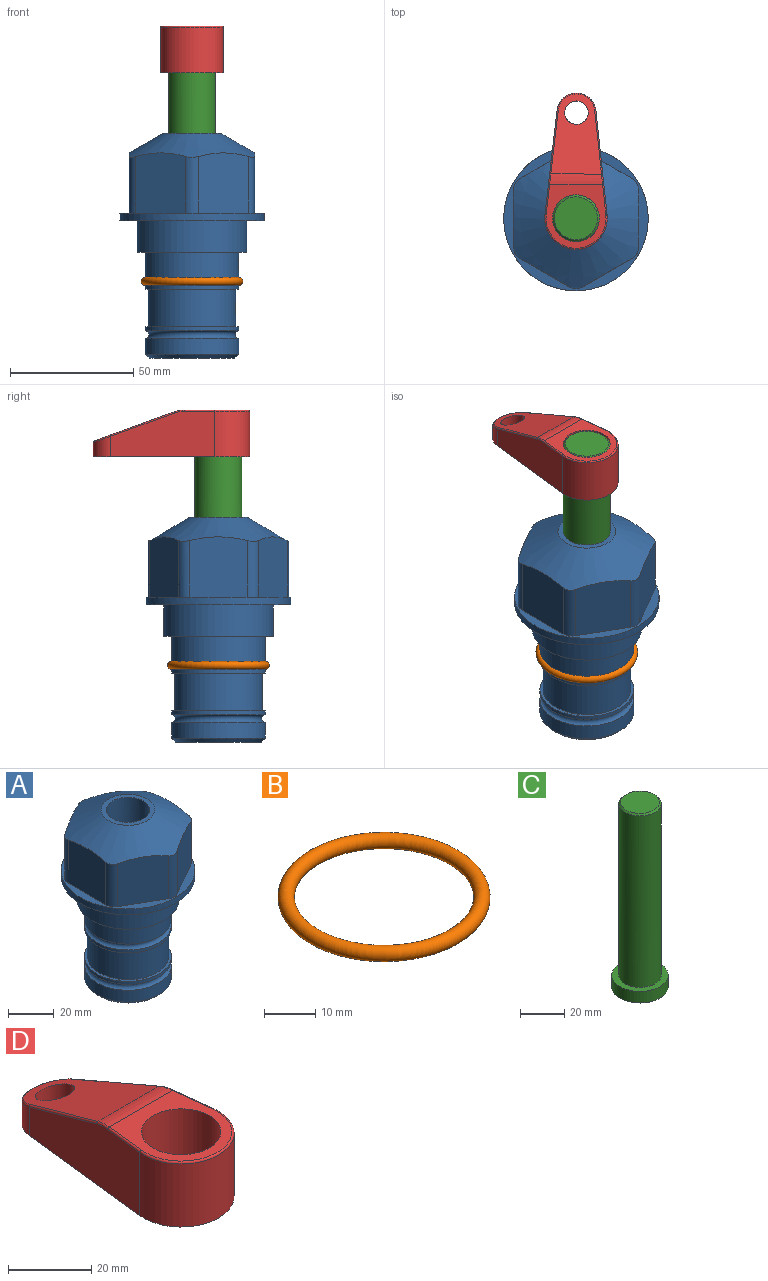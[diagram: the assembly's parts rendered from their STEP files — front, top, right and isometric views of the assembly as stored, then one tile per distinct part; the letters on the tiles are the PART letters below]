
ASSEMBLY  parts=4 mates=2
PART A: 36 faces, bbox 58.7x58.7x91.2 mm
  f0: cylinder r=17.78mm len=35.56mm, axis (0,0,1), area 1670.8mm2, adj f23,f24,f31
  f1: cylinder r=19.05mm len=38.1mm, axis (0,0,1), area 1191.9mm2, adj f26,f27,f30
  f2: plane 58.66x58.66mm, normal (0,0,-1), area 1150.6mm2, adj f3,f28
  f3: cylinder r=29.33mm len=58.66mm, axis (0,0,-1), area 585.1mm2, adj f2,f4
  f4: plane 58.66x58.66mm, normal (0,0,1), area 475.9mm2, adj f3,f5,f6,f7,f8,f9,f10,f11
  f5: plane 24.5x20.32mm, normal (-0.5,0.87,0), area 562.8mm2, adj f4,f15,f16,f17
  f6: plane 24.5x20.32mm, normal (0.5,0.87,0), area 562.8mm2, adj f4,f14,f15,f17
  f7: plane 24.5x23.48mm, normal (1,0,0), area 562.8mm2, adj f4,f13,f14,f17
  f8: plane 24.5x20.32mm, normal (0.5,-0.87,0), area 562.8mm2, adj f4,f12,f13,f17
  f9: plane 24.5x20.32mm, normal (-0.5,-0.87,0), area 562.8mm2, adj f4,f11,f12,f17
  f10: plane 24.5x23.48mm, normal (-1,0,0), area 562.8mm2, adj f4,f11,f16,f17
  f11: cylinder r=5.08mm len=23.01mm, axis (0,0,-1), area 121.2mm2, adj f4,f9,f10,f17
  f12: cylinder r=5.08mm len=23.01mm, axis (0,0,-1), area 121.2mm2, adj f4,f8,f9,f17
  f13: cylinder r=5.08mm len=23.01mm, axis (0,0,-1), area 121.2mm2, adj f4,f7,f8,f17
  f14: cylinder r=5.08mm len=23.01mm, axis (0,0,-1), area 121.2mm2, adj f4,f6,f7,f17
  f15: cylinder r=5.08mm len=23.01mm, axis (0,0,-1), area 121.2mm2, adj f4,f5,f6,f17
  f16: cylinder r=5.08mm len=23.01mm, axis (0,0,-1), area 121.2mm2, adj f4,f5,f10,f17
  f17: cone r=11.73mm half-angle=60deg, axis (0,0,-1), area 2071.8mm2, adj f5,f6,f7,f8,f9,f10,f11,f12
  f18: plane 23.46x23.46mm, normal (0,0,1), area 147.4mm2, adj f17,f35
  f19: plane 34.93x34.93mm, normal (0,0,-1), area 958mm2, adj f29
  f20: cylinder r=19.05mm len=38.1mm, axis (0,0,1), area 760.1mm2, adj f21,f29
  f21: torus R=19.05mm, axis (0,0,1), area 565.3mm2, adj f20,f22
  f22: cylinder r=19.05mm len=38.1mm, axis (0,0,1), area 190mm2, adj f21,f23
  f23: plane 38.1x38.1mm, normal (0,0,1), area 146.9mm2, adj f0,f22
  f24: plane 38.1x38.1mm, normal (0,0,-1), area 146.9mm2, adj f0,f25
  f25: cylinder r=19.05mm len=38.1mm, axis (0,0,1), area 190mm2, adj f24,f26
  f26: torus R=19.05mm, axis (0,0,1), area 565.3mm2, adj f1,f25
  f27: plane 44.45x44.45mm, normal (0,0,-1), area 411.7mm2, adj f1,f28
  f28: cylinder r=22.23mm len=44.45mm, axis (0,0,1), area 1773.5mm2, adj f2,f27
  f29: cone r=19.05mm half-angle=45deg, axis (0,0,1), area 257.5mm2, adj f19,f20
  f30: cylinder r=3.17mm len=6.75mm, axis (-1,0,0), area 128mm2, adj f1,f33
  f31: cylinder r=3.17mm len=6.35mm, axis (-1,0,0), area 102.5mm2, adj f0,f33
  f32: plane 25.4x25.4mm, normal (0,0,1), area 506.7mm2, adj f33
  f33: cylinder r=12.7mm len=66.42mm, axis (0,0,-1), area 5236.2mm2, adj f30,f31,f32,f34
  f34: cone r=9.53mm half-angle=30deg, axis (0,0,-1), area 443.4mm2, adj f33,f35
  f35: cylinder r=9.53mm len=19.05mm, axis (0,0,-1), area 849mm2, adj f18,f34
PART B: 1 faces, bbox 44.7x44.7x3.2 mm
  f0: torus R=19.05mm, axis (0,0,1), area 1193.9mm2
PART C: 6 faces, bbox 25.4x25.4x101.6 mm
  f0: plane 17.46x17.46mm, normal (0,0,1), area 239.5mm2, adj f5
  f1: plane 25.4x25.4mm, normal (0,0,-1), area 506.7mm2, adj f2
  f2: cylinder r=12.7mm len=25.4mm, axis (0,0,1), area 506.7mm2, adj f1,f3
  f3: plane 25.4x25.4mm, normal (0,0,1), area 221.7mm2, adj f2,f4
  f4: cylinder r=9.53mm len=94.46mm, axis (0,0,1), area 5653mm2, adj f3,f5
  f5: cone r=8.73mm half-angle=45deg, axis (0,0,-1), area 64.4mm2, adj f0,f4
PART D: 44 faces, bbox 27.5x64.5x19.1 mm
  f0: plane 2.3x0.95mm, normal (0,0,-1), area 1mm2, adj f25,f30,f34
  f1: plane 63.5x25.4mm, normal (0,0,-1), area 561.7mm2, adj f2,f3,f4,f5,f6,f7,f19,f20
  f2: cylinder r=12.7mm len=25.4mm, axis (0,0,-1), area 792.2mm2, adj f1,f3,f5,f13
  f3: plane 42.33x18.54mm, normal (0.99,0.11,0), area 647mm2, adj f1,f2,f4,f11,f12,f14
  f4: cylinder r=7.94mm len=15.78mm, axis (0,0,-1), area 158.6mm2, adj f1,f3,f5,f16
  f5: plane 42.33x18.54mm, normal (-0.99,0.11,0), area 647mm2, adj f1,f2,f4,f15,f17,f18
  f6: cylinder r=9.53mm len=19.05mm, axis (0,0,-1), area 1140.1mm2, adj f1,f8
  f7: cylinder r=4.76mm len=10.98mm, axis (0,0,-1), area 276.1mm2, adj f1,f9
  f8: plane 25.83x24.38mm, normal (0,0,1), area 262.2mm2, adj f6,f10,f11,f13,f15
  f9: plane 32.49x20.55mm, normal (0,0.34,0.94), area 489.9mm2, adj f7,f10,f14,f16,f18
  f10: cylinder r=12.7mm len=21.49mm, axis (-1,0,0), area 93.2mm2, adj f8,f9,f12,f17
  f11: cylinder r=0.51mm len=12.34mm, axis (0.11,-0.99,0), area 9.9mm2, adj f3,f8,f12,f13
  f12: bspline ~7.62x1.64mm, area 3.5mm2, adj f3,f10,f11,f14
  f13: torus R=12.19mm, axis (0,0,1), area 33.6mm2, adj f2,f8,f11,f15
  f14: cylinder r=0.51mm len=26.01mm, axis (0.1,-0.93,0.34), area 21.6mm2, adj f3,f9,f12,f16
  f15: cylinder r=0.51mm len=12.34mm, axis (0.11,0.99,0), area 9.9mm2, adj f5,f8,f13,f17
  f16: bspline ~15.78x7.05mm, area 15.7mm2, adj f4,f9,f14,f18
  f17: bspline ~7.62x1.64mm, area 3.5mm2, adj f5,f10,f15,f18
  f18: cylinder r=0.51mm len=26.01mm, axis (0.1,0.93,-0.34), area 21.6mm2, adj f5,f9,f16,f17
  f19: plane 21.6x14.29mm, normal (-0.99,-0.11,0), area 242.6mm2, adj f1,f26,f28,f34,f36,f38
  f20: plane 21.6x14.29mm, normal (0.99,-0.11,0), area 242.6mm2, adj f1,f27,f29,f37,f39,f41
  f21: cylinder r=12.7mm len=14.29mm, axis (0,0,-1), area 173.2mm2, adj f1,f26,f27,f30,f31,f33
  f22: cylinder r=7.94mm len=7.63mm, axis (0,0,-1), area 53.8mm2, adj f1,f28,f29,f42
  f23: plane 2.3x0.95mm, normal (0,0,-1), area 1mm2, adj f25,f33,f37
  f24: plane 17.94x12.32mm, normal (0,-0.34,-0.94), area 191.2mm2, adj f25,f38,f41,f42
  f25: cylinder r=9.53mm len=12.93mm, axis (-1,0,0), area 37.5mm2, adj f0,f23,f24,f31,f36,f39
  f26: cylinder r=1.59mm len=14.29mm, axis (0,0,-1), area 49mm2, adj f1,f19,f21,f32
  f27: cylinder r=1.59mm len=14.29mm, axis (0,0,-1), area 49mm2, adj f1,f20,f21,f35
  f28: cylinder r=1.59mm len=7.28mm, axis (0,0,-1), area 22.1mm2, adj f1,f19,f22,f40
  f29: cylinder r=1.59mm len=7.28mm, axis (0,0,-1), area 22.1mm2, adj f1,f20,f22,f43
  f30: torus R=14.29mm, axis (0,0,1), area 5.8mm2, adj f0,f21,f31,f32
  f31: bspline ~11.06x2.73mm, area 20.8mm2, adj f21,f25,f30,f33
  f32: sphere r=1.59mm, area 5.4mm2, adj f26,f30,f34
  f33: torus R=14.29mm, axis (0,0,1), area 5.8mm2, adj f21,f23,f31,f35
  f34: cylinder r=1.59mm len=1.68mm, axis (-0.11,0.99,0), area 2.4mm2, adj f0,f19,f32,f36
  f35: sphere r=1.59mm, area 5.4mm2, adj f27,f33,f37
  f36: bspline ~5.82x2.33mm, area 7.7mm2, adj f19,f25,f34,f38
  f37: cylinder r=1.59mm len=1.68mm, axis (0.11,0.99,0), area 2.4mm2, adj f20,f23,f35,f39
  f38: cylinder r=1.59mm len=18.33mm, axis (0.1,-0.93,0.34), area 46.7mm2, adj f19,f24,f36,f40
  f39: bspline ~5.82x2.33mm, area 7.7mm2, adj f20,f25,f37,f41
  f40: sphere r=1.59mm, area 3.6mm2, adj f28,f38,f42
  f41: cylinder r=1.59mm len=18.33mm, axis (0.1,0.93,-0.34), area 46.7mm2, adj f20,f24,f39,f43
  f42: bspline ~8.31x1.84mm, area 15.3mm2, adj f22,f24,f40,f43
  f43: sphere r=1.59mm, area 3.6mm2, adj f29,f41,f42
PLACE A at identity fixed
PLACE B at identity
PLACE C rot(axis=(0,0,-1),0.3deg) t=(0,0,5.49)mm
PLACE D rot(axis=(0,0,-1),0.3deg) t=(0,0,60.1)mm
MATE cylindrical C.f2 <-> A.f0  axis (0,0,1) through (0,0,31.13)mm
MATE fastened D.f2 <-> C.f2  axis (0,0,-1) through (0,0,79.15)mm
